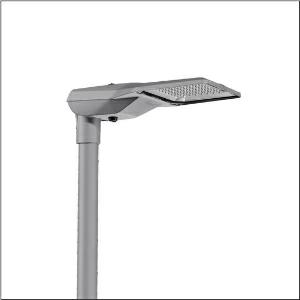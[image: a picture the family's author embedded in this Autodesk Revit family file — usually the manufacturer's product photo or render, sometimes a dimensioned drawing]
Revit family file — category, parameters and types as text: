
# Revit family: streetlight_sl_21_iq_midi___st0_8a_5xe3c31y08mb_7afc
name_source: partatom
category: Lighting Fixtures
units: mm (PartAtom-declared; Revit-internal decimal feet)

## family parameters
Cut with Voids When Loaded = No
Host = Face
Light Source = No
Part Type = Normal
Room Calculation Point = No
Round Connector Dimension = Use Diameter
Shared = No

## types (1)
- --- (1 x LED, 18340 lm, 129.3 W, 3000K)
    Apparent Load = 129 VA
    CIE Flux Codes = 38 75 97 100 100
    Color Rendering = 70
    Color Temperature = 3000K
    Default Elevation = 1800 mm
    Description = Streetlight SL 21 iQ midi, mast luminaire, primary light control with lens, of PMMA, primary optical cover: cover, of toughened safety glass, transparent, light distribution: ST0.8a, light emission: direct distribution, primary light characteristic: asymmetric, installation type: post-top, side-entry, LED, High Power LED, rated luminous flux: 18.340lm, luminous efficacy: 142lm/W, light colour: 730, colour temperature: 3000K, control gear: iQ-Street Remote, D4i with power reduction, control: pre-setting: logarithmic dimming characteristic, Street-Remote, Auto-Match, Temp-Guard, Lumen-Switch, Night-Set, Smart-Wire, Light-Fading, Desk-Remote (wireless, voltage-free reading and setting of iQ features in the workshop via application-optimized NFC function/RFID function), optimised constant luminous flux control (CLO 2.0), mains connection: 230..240V, AC, 50/60Hz, start of lifetime: 129W, end of service life: 142W, reduction: 56W, luminaire housing, of diecast aluminium, powder-coated, SITECO metallic grey (DB 702S), corrosivity category C5 high according to DIN EN ISO 12944, please order mast flange separately, inclination adjustable: 0°, 5°, 10°, 15°, sealing non-destructively replaceable, multi-level sealing system, length: 644mm, width: 335mm, height: 110mm, mast flange for spigot size: 42mm (side-entry): 5XC10008XM4, 60/48mm (side-entry/post-top): 5XC10108XM2, 76/60mm (side-entry/post-top): 5XC10108XM1, mounting height: 4..8m, Smart Interface below and above, protection rating (complete): IP66, insulation class (complete): insulation class II (safety insulation), certification: CE, ENEC, ENEC+, VDE, impact resistance: IK10, permissible operating ambient temperature for outdoor applications: -40..+50°C, standard-compliant lighting for roads and squares, packaging unit: 1 piece

Light Distribution: ST0.8a
    Height = 111 mm
    Lamp = 1 x LED
    Lamp Light Flux = 18340 lm
    Lamp Power = 129.3 W
    Lamp count = 1
    Length = 644 mm
    Luminous efficacy = 142 lm/W
    Manufacturer = Siteco
    ModVariant = No
    Model = 5XE3C31Y08MB
    Mounting Place = Pole
    Mounting Type = Pole top
    Number of Poles = 1
    OnlyDefault = Yes
    Power Factor = 1
    Product Name = Streetlight SL 21 iQ midi | ST0.8a
    Product group = mast luminaire | pylon top
    ProductGroupID = 6100
    Protection Class = Protection class II
    Protection Degree = IP 66
    RLX_Detail_Level = 1
    RLX_Emergency_Light_Flux = 0 lm
    RLX_Emergency_Type = 0
    RLX_Emergency_Type_DB = No
    RlxData = <blob elided: 90829 chars, md5=b53b5a2b>
    Socket = socket
    Standby Power = 0 W
    System Light Flux = 18340 lm
    System Power = 129 W
    Type Comments = factory setting: luminous flux: 100 % | dim-lin: 254 | 672 mA
    Type Image = l_1004304.jpg
    URL = http://relux.com
    VarID = @adj_114949
    Voltage = 0 V
    Weight = 0.00 kg
    Width = 336 mm

## geometry (parser evidence)
native form markers: Blend x4, Sweep x10
no freeform markers — native parametric forms only
